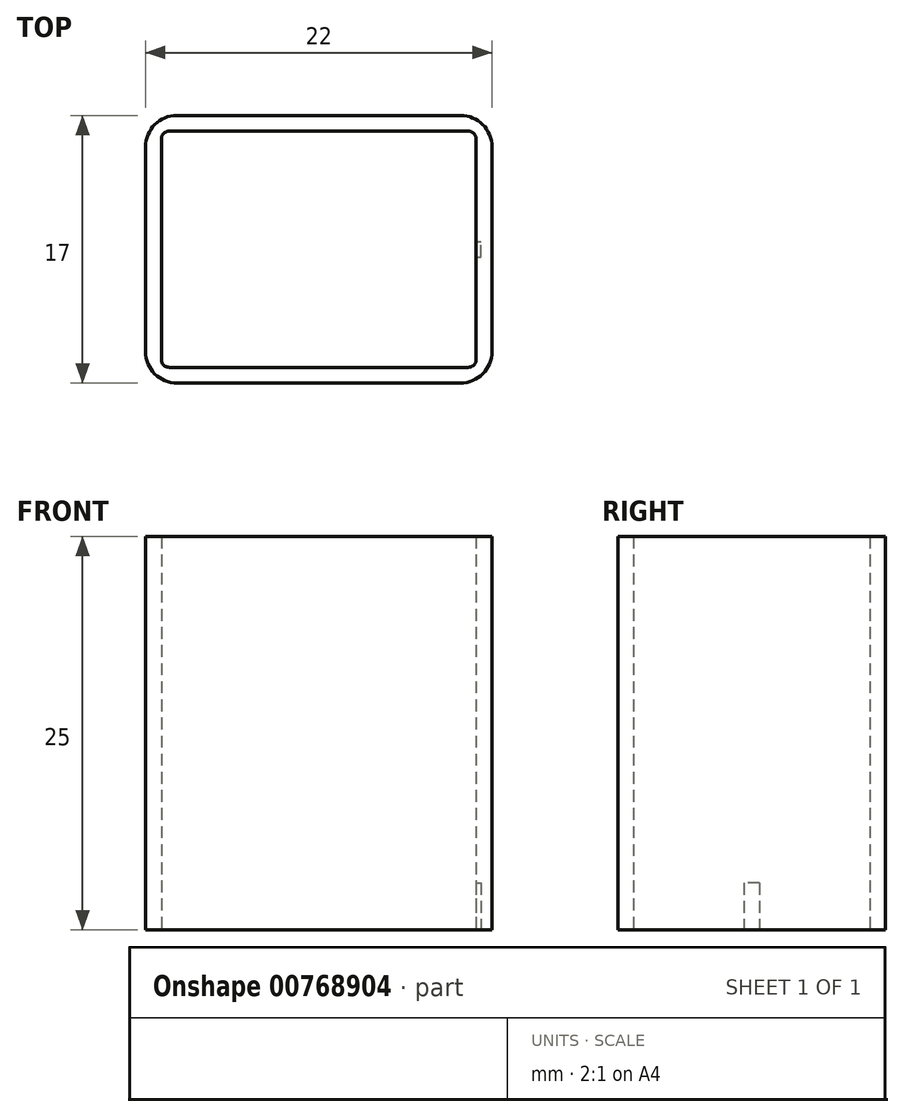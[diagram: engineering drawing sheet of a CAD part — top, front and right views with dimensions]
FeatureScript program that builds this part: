
annotation { "Feature Type Name" : "Feature", "Feature Type Description" : "" }
export const myFeature = defineFeature(function(context is Context, id is Id, definition is map)
    precondition{}
    {
        {
            var Q0;
            Q0=qCreatedBy(makeId("Top.planeOp"),FACE);
            var sketch = newSketch(context, id + "F0", { "sketchPlane" : qUnion([Q0])});
            skLineSegment(sketch, "E0.bottom", {"start": v(0, 0) * mm, "end": v(22, 0) * mm});
            skLineSegment(sketch, "E0.top", {"start": v(0, 17) * mm, "end": v(22, 17) * mm});
            skLineSegment(sketch, "E0.left", {"start": v(0, 0) * mm, "end": v(0, 17) * mm});
            skLineSegment(sketch, "E0.right", {"start": v(22, 0) * mm, "end": v(22, 17) * mm});
            skLineSegment(sketch, "E1.bottom", {"start": v(1, 16) * mm, "end": v(21, 16) * mm});
            skLineSegment(sketch, "E1.top", {"start": v(1, 1) * mm, "end": v(21, 1) * mm});
            skLineSegment(sketch, "E1.left", {"start": v(1, 16) * mm, "end": v(1, 1) * mm});
            skLineSegment(sketch, "E1.right", {"start": v(21, 16) * mm, "end": v(21, 1) * mm});
            skSolve(sketch);
        }
        {
            var Q0;
            Q0 = qSketchRegion(id + "F0", true);
            extrude(context, id + "F1", {"entities" : qUnion([Q0]), "depth" : 25 * mm, "offsetDistance" : 25 * mm});
        }
        {
            var Q0;
            Q0=makeQuery(id+"F1.opExtrude","SWEPT_EDGE",EDGE,{"disambiguationData":[OSD([sQuery(id+"F0.wireOp",EDGE,"E0.top"),sQuery(id+"F0.wireOp",EDGE,"E0.left")])]});
            var Q1;
            Q1=makeQuery(id+"F1.opExtrude","SWEPT_EDGE",EDGE,{"disambiguationData":[OSD([sQuery(id+"F0.wireOp",EDGE,"E0.bottom"),sQuery(id+"F0.wireOp",EDGE,"E0.left")])]});
            var Q2;
            Q2=makeQuery(id+"F1.opExtrude","SWEPT_EDGE",EDGE,{"disambiguationData":[OSD([sQuery(id+"F0.wireOp",EDGE,"E0.bottom"),sQuery(id+"F0.wireOp",EDGE,"E0.right")])]});
            var Q3;
            Q3=makeQuery(id+"F1.opExtrude","SWEPT_EDGE",EDGE,{"disambiguationData":[OSD([sQuery(id+"F0.wireOp",EDGE,"E0.top"),sQuery(id+"F0.wireOp",EDGE,"E0.right")])]});
            fillet(context, id + "F2", {"entities" : qUnion([Q0, Q1, Q2, Q3]), "radius" : 2 * mm, "tangentPropagation" : true, "allowEdgeOverflow" : false});
        }
        {
            var Q0;
            Q0=makeQuery(id+"F1.opExtrude","CAP_FACE",FACE,{"disambiguationData":[OSD([sQuery(id+"F0.wireOp",EDGE,"E0.bottom"),sQuery(id+"F0.wireOp",EDGE,"E0.top"),sQuery(id+"F0.wireOp",EDGE,"E0.left"),sQuery(id+"F0.wireOp",EDGE,"E0.right"),sQuery(id+"F0.wireOp",EDGE,"E1.bottom"),sQuery(id+"F0.wireOp",EDGE,"E1.top"),sQuery(id+"F0.wireOp",EDGE,"E1.left"),sQuery(id+"F0.wireOp",EDGE,"E1.right")])],"isStart":true});
            var sketch = newSketch(context, id + "F3", { "sketchPlane" : qUnion([Q0])});
            skLineSegment(sketch, "E2.bottom", {"start": v(21, -8) * mm, "end": v(21.3, -8) * mm});
            skLineSegment(sketch, "E2.top", {"start": v(21, -9) * mm, "end": v(21.3, -9) * mm});
            skLineSegment(sketch, "E2.left", {"start": v(21, -8) * mm, "end": v(21, -9) * mm});
            skLineSegment(sketch, "E2.right", {"start": v(21.3, -8) * mm, "end": v(21.3, -9) * mm});
            skSolve(sketch);
        }
        {
            var Q0;
            Q0 = qSketchRegion(id + "F3", true);
            extrude(context, id + "F4", {"entities" : qUnion([Q0]), "operationType" : NewBodyOperationType.REMOVE, "oppositeDirection" : true, "depth" : 3 * mm, "offsetDistance" : 25 * mm});
        }
        {
            var Q0;
            Q0=makeQuery(id+"F1.opExtrude","SWEPT_EDGE",EDGE,{"disambiguationData":[OSD([sQuery(id+"F0.wireOp",EDGE,"E1.top"),sQuery(id+"F0.wireOp",EDGE,"E1.right")])]});
            var Q1;
            Q1=makeQuery(id+"F1.opExtrude","SWEPT_EDGE",EDGE,{"disambiguationData":[OSD([sQuery(id+"F0.wireOp",EDGE,"E1.top"),sQuery(id+"F0.wireOp",EDGE,"E1.left")])]});
            var Q2;
            Q2=makeQuery(id+"F1.opExtrude","SWEPT_EDGE",EDGE,{"disambiguationData":[OSD([sQuery(id+"F0.wireOp",EDGE,"E1.bottom"),sQuery(id+"F0.wireOp",EDGE,"E1.left")])]});
            var Q3;
            Q3=makeQuery(id+"F1.opExtrude","SWEPT_EDGE",EDGE,{"disambiguationData":[OSD([sQuery(id+"F0.wireOp",EDGE,"E1.bottom"),sQuery(id+"F0.wireOp",EDGE,"E1.right")])]});
            fillet(context, id + "F5", {"entities" : qUnion([Q0, Q1, Q2, Q3]), "radius" : .5 * mm, "tangentPropagation" : true, "allowEdgeOverflow" : false});
        }
    });
